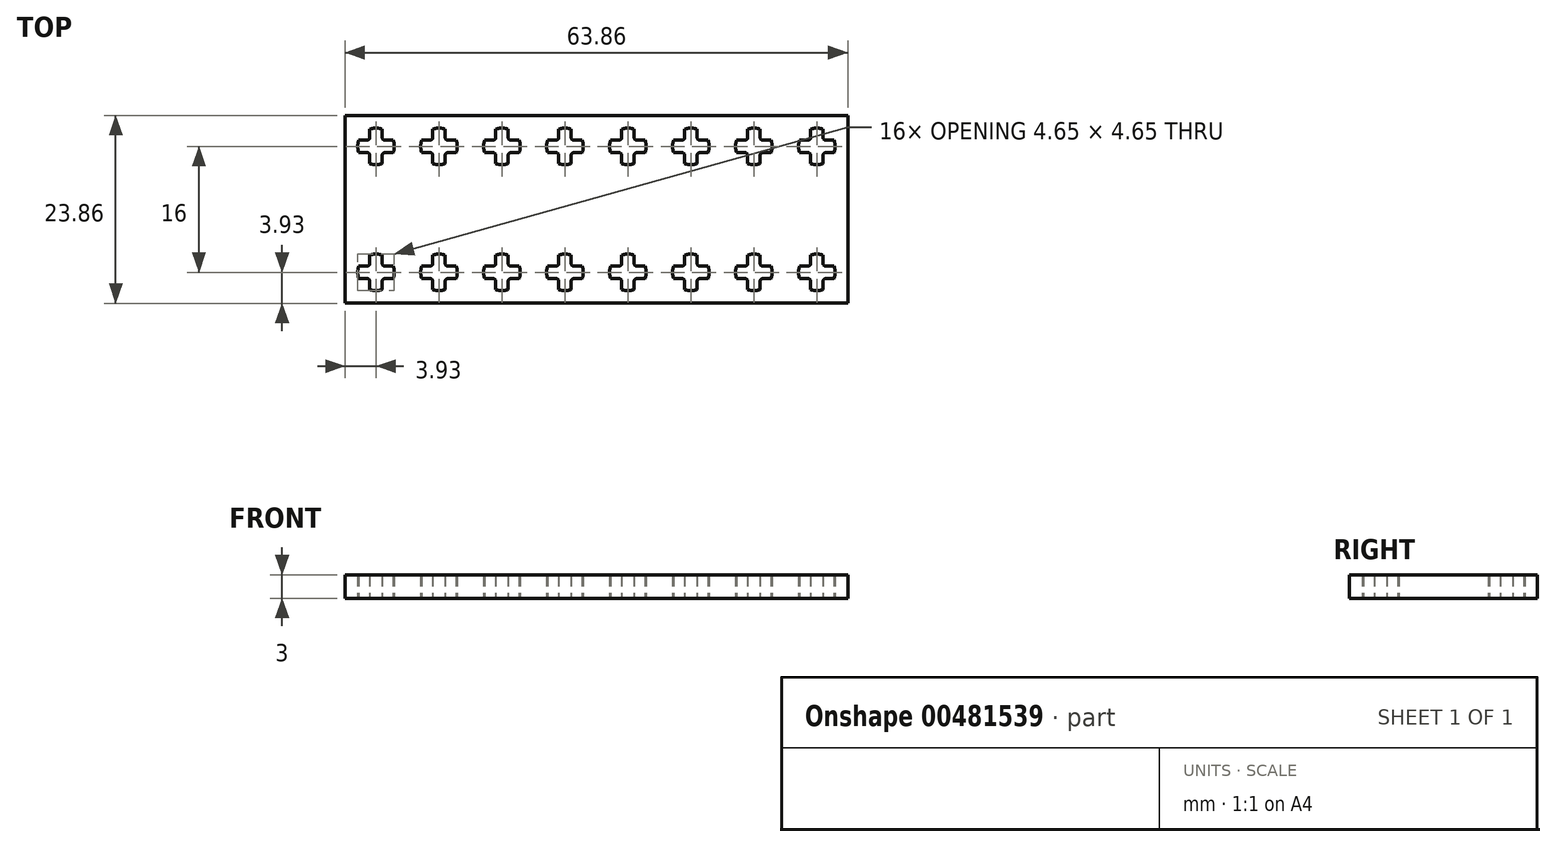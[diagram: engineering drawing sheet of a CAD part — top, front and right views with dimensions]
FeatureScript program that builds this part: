
annotation { "Feature Type Name" : "Feature", "Feature Type Description" : "" }
export const myFeature = defineFeature(function(context is Context, id is Id, definition is map)
    precondition{}
    {
        {
            var Q0;
            Q0=qCreatedBy(makeId("Top.planeOp"),FACE);
            var sketch = newSketch(context, id + "F0", { "sketchPlane" : qUnion([Q0])});
            skLineSegment(sketch, "E0.bottom", {"start": v(-32, 12) * mm, "end": v(32, 12) * mm, "construction": true});
            skLineSegment(sketch, "E0.top", {"start": v(-32, -12) * mm, "end": v(32, -12) * mm, "construction": true});
            skLineSegment(sketch, "E0.left", {"start": v(-32, 12) * mm, "end": v(-32, -12) * mm, "construction": true});
            skLineSegment(sketch, "E0.right", {"start": v(32, 12) * mm, "end": v(32, -12) * mm, "construction": true});
            skLineSegment(sketch, "E1", {"start": v(-28.8, 10.18) * mm, "end": v(-27.2, 10.18) * mm, "construction": true});
            skLineSegment(sketch, "E2", {"start": v(-27.2, 10.18) * mm, "end": v(-27.2, 9.1) * mm});
            skLineSegment(sketch, "E3", {"start": v(-26.9, 8.8) * mm, "end": v(-25.82, 8.8) * mm});
            skLineSegment(sketch, "E4", {"start": v(-25.82, 8.8) * mm, "end": v(-28, 8) * mm, "construction": true});
            skLineSegment(sketch, "E5", {"start": v(-28, 8) * mm, "end": v(-28.8, 10.18) * mm, "construction": true});
            skArc(sketch, "E6", {"start": v(-27.2, 10.18) * mm, "mid": v(-28, 10.33) * mm, "end": v(-28.8, 10.18) * mm});
            skArc(sketch, "E7", {"start": v(-27.2, 9.1) * mm, "mid": v(-27.11, 8.89) * mm, "end": v(-26.9, 8.8) * mm});
            skLineSegment(sketch, "E8", {"start": v(-27.2, 10.18) * mm, "end": v(-27.2, 8.8) * mm, "construction": true});
            skLineSegment(sketch, "E9", {"start": v(-27.2, 8.8) * mm, "end": v(-25.82, 8.8) * mm, "construction": true});
            skArc(sketch, "E10.1.0", {"start": v(-30.18, 8.8) * mm, "mid": v(-30.32, 8) * mm, "end": v(-30.18, 7.2) * mm});
            skArc(sketch, "E10.1.1", {"start": v(-29.1, 8.8) * mm, "mid": v(-28.89, 8.89) * mm, "end": v(-28.8, 9.1) * mm});
            skLineSegment(sketch, "E10.1.2", {"start": v(-30.18, 8.8) * mm, "end": v(-29.1, 8.8) * mm});
            skLineSegment(sketch, "E10.1.3", {"start": v(-28.8, 9.1) * mm, "end": v(-28.8, 10.18) * mm});
            skArc(sketch, "E10.2.0", {"start": v(-28.8, 5.82) * mm, "mid": v(-28, 5.68) * mm, "end": v(-27.2, 5.82) * mm});
            skArc(sketch, "E10.2.1", {"start": v(-28.8, 6.9) * mm, "mid": v(-28.89, 7.11) * mm, "end": v(-29.1, 7.2) * mm});
            skLineSegment(sketch, "E10.2.2", {"start": v(-28.8, 5.82) * mm, "end": v(-28.8, 6.9) * mm});
            skLineSegment(sketch, "E10.2.3", {"start": v(-29.1, 7.2) * mm, "end": v(-30.18, 7.2) * mm});
            skArc(sketch, "E10.3.0", {"start": v(-25.82, 7.2) * mm, "mid": v(-25.67, 8) * mm, "end": v(-25.82, 8.8) * mm});
            skArc(sketch, "E10.3.1", {"start": v(-26.9, 7.2) * mm, "mid": v(-27.11, 7.11) * mm, "end": v(-27.2, 6.9) * mm});
            skLineSegment(sketch, "E10.3.2", {"start": v(-25.82, 7.2) * mm, "end": v(-26.9, 7.2) * mm});
            skLineSegment(sketch, "E10.3.3", {"start": v(-27.2, 6.9) * mm, "end": v(-27.2, 5.82) * mm});
            skArc(sketch, "E11.1.0.0", {"start": v(-19.2, 10.18) * mm, "mid": v(-20, 10.32) * mm, "end": v(-20.8, 10.18) * mm});
            skArc(sketch, "E11.1.0.1", {"start": v(-18.9, 7.2) * mm, "mid": v(-19.11, 7.11) * mm, "end": v(-19.2, 6.9) * mm});
            skLineSegment(sketch, "E11.1.0.2", {"start": v(-17.82, 7.2) * mm, "end": v(-18.9, 7.2) * mm});
            skLineSegment(sketch, "E11.1.0.3", {"start": v(-21.1, 7.2) * mm, "end": v(-22.18, 7.2) * mm});
            skArc(sketch, "E11.1.0.4", {"start": v(-20.8, 6.9) * mm, "mid": v(-20.89, 7.11) * mm, "end": v(-21.1, 7.2) * mm});
            skLineSegment(sketch, "E11.1.0.5", {"start": v(-20.8, 9.1) * mm, "end": v(-20.8, 10.18) * mm});
            skLineSegment(sketch, "E11.1.0.6", {"start": v(-22.18, 8.8) * mm, "end": v(-21.1, 8.8) * mm});
            skArc(sketch, "E11.1.0.7", {"start": v(-21.1, 8.8) * mm, "mid": v(-20.89, 8.89) * mm, "end": v(-20.8, 9.1) * mm});
            skArc(sketch, "E11.1.0.8", {"start": v(-20.8, 5.82) * mm, "mid": v(-20, 5.67) * mm, "end": v(-19.2, 5.82) * mm});
            skArc(sketch, "E11.1.0.9", {"start": v(-22.18, 8.8) * mm, "mid": v(-22.32, 8) * mm, "end": v(-22.18, 7.2) * mm});
            skPoint(sketch, "E11.1.0.10", {"position": v(-20, 8) * mm});
            skLineSegment(sketch, "E11.1.0.11", {"start": v(-20.8, 5.82) * mm, "end": v(-20.8, 6.9) * mm});
            skArc(sketch, "E11.1.0.12", {"start": v(-17.82, 7.2) * mm, "mid": v(-17.67, 8) * mm, "end": v(-17.82, 8.8) * mm});
            skLineSegment(sketch, "E11.1.0.13", {"start": v(-19.2, 6.9) * mm, "end": v(-19.2, 5.82) * mm});
            skLineSegment(sketch, "E11.1.0.14", {"start": v(-19.2, 10.18) * mm, "end": v(-19.2, 9.1) * mm});
            skLineSegment(sketch, "E11.1.0.15", {"start": v(-18.9, 8.8) * mm, "end": v(-17.82, 8.8) * mm});
            skArc(sketch, "E11.1.0.16", {"start": v(-19.2, 9.1) * mm, "mid": v(-19.11, 8.89) * mm, "end": v(-18.9, 8.8) * mm});
            skArc(sketch, "E11.2.0.0", {"start": v(-11.2, 10.18) * mm, "mid": v(-12, 10.32) * mm, "end": v(-12.8, 10.18) * mm});
            skArc(sketch, "E11.2.0.1", {"start": v(-10.9, 7.2) * mm, "mid": v(-11.11, 7.11) * mm, "end": v(-11.2, 6.9) * mm});
            skLineSegment(sketch, "E11.2.0.2", {"start": v(-9.82, 7.2) * mm, "end": v(-10.9, 7.2) * mm});
            skLineSegment(sketch, "E11.2.0.3", {"start": v(-13.1, 7.2) * mm, "end": v(-14.18, 7.2) * mm});
            skArc(sketch, "E11.2.0.4", {"start": v(-12.8, 6.9) * mm, "mid": v(-12.89, 7.11) * mm, "end": v(-13.1, 7.2) * mm});
            skLineSegment(sketch, "E11.2.0.5", {"start": v(-12.8, 9.1) * mm, "end": v(-12.8, 10.18) * mm});
            skLineSegment(sketch, "E11.2.0.6", {"start": v(-14.18, 8.8) * mm, "end": v(-13.1, 8.8) * mm});
            skArc(sketch, "E11.2.0.7", {"start": v(-13.1, 8.8) * mm, "mid": v(-12.89, 8.89) * mm, "end": v(-12.8, 9.1) * mm});
            skArc(sketch, "E11.2.0.8", {"start": v(-12.8, 5.82) * mm, "mid": v(-12, 5.67) * mm, "end": v(-11.2, 5.82) * mm});
            skArc(sketch, "E11.2.0.9", {"start": v(-14.18, 8.8) * mm, "mid": v(-14.32, 8) * mm, "end": v(-14.18, 7.2) * mm});
            skPoint(sketch, "E11.2.0.10", {"position": v(-12, 8) * mm});
            skLineSegment(sketch, "E11.2.0.11", {"start": v(-12.8, 5.82) * mm, "end": v(-12.8, 6.9) * mm});
            skArc(sketch, "E11.2.0.12", {"start": v(-9.82, 7.2) * mm, "mid": v(-9.67, 8) * mm, "end": v(-9.82, 8.8) * mm});
            skLineSegment(sketch, "E11.2.0.13", {"start": v(-11.2, 6.9) * mm, "end": v(-11.2, 5.82) * mm});
            skLineSegment(sketch, "E11.2.0.14", {"start": v(-11.2, 10.18) * mm, "end": v(-11.2, 9.1) * mm});
            skLineSegment(sketch, "E11.2.0.15", {"start": v(-10.9, 8.8) * mm, "end": v(-9.82, 8.8) * mm});
            skArc(sketch, "E11.2.0.16", {"start": v(-11.2, 9.1) * mm, "mid": v(-11.11, 8.89) * mm, "end": v(-10.9, 8.8) * mm});
            skLineSegment(sketch, "E11.direction1", {"start": v(-28.8, 5.82) * mm, "end": v(-20.8, 5.82) * mm, "construction": true});
            skLineSegment(sketch, "E11.direction2", {"start": v(-28.8, 5.82) * mm, "end": v(-28.8, -2.18) * mm, "construction": true});
            skLineSegment(sketch, "E12.bottom", {"start": v(-31.92, 11.93) * mm, "end": v(31.93, 11.92) * mm});
            skLineSegment(sketch, "E12.top", {"start": v(-31.93, -11.92) * mm, "end": v(31.92, -11.93) * mm});
            skLineSegment(sketch, "E12.left", {"start": v(-31.92, 11.93) * mm, "end": v(-31.93, -11.92) * mm});
            skLineSegment(sketch, "E12.right", {"start": v(31.93, 11.92) * mm, "end": v(31.93, -11.92) * mm});
            skArc(sketch, "E13.0.3.0", {"start": v(-3.2, 10.18) * mm, "mid": v(-4, 10.32) * mm, "end": v(-4.8, 10.18) * mm});
            skArc(sketch, "E13.4.3.0", {"start": v(-2.9, 7.2) * mm, "mid": v(-3.11, 7.11) * mm, "end": v(-3.2, 6.9) * mm});
            skLineSegment(sketch, "E13.8.3.0", {"start": v(-1.82, 7.2) * mm, "end": v(-2.9, 7.2) * mm});
            skLineSegment(sketch, "E13.11.3.0", {"start": v(-5.1, 7.2) * mm, "end": v(-6.18, 7.2) * mm});
            skArc(sketch, "E13.14.3.0", {"start": v(-4.8, 6.9) * mm, "mid": v(-4.89, 7.11) * mm, "end": v(-5.1, 7.2) * mm});
            skLineSegment(sketch, "E13.18.3.0", {"start": v(-4.8, 9.1) * mm, "end": v(-4.8, 10.18) * mm});
            skLineSegment(sketch, "E13.21.3.0", {"start": v(-6.18, 8.8) * mm, "end": v(-5.1, 8.8) * mm});
            skArc(sketch, "E13.24.3.0", {"start": v(-5.1, 8.8) * mm, "mid": v(-4.89, 8.89) * mm, "end": v(-4.8, 9.1) * mm});
            skArc(sketch, "E13.28.3.0", {"start": v(-4.8, 5.82) * mm, "mid": v(-4, 5.67) * mm, "end": v(-3.2, 5.82) * mm});
            skArc(sketch, "E13.32.3.0", {"start": v(-6.18, 8.8) * mm, "mid": v(-6.32, 8) * mm, "end": v(-6.18, 7.2) * mm});
            skPoint(sketch, "E13.36.3.0", {"position": v(-4, 8) * mm});
            skLineSegment(sketch, "E13.37.3.0", {"start": v(-4.8, 5.82) * mm, "end": v(-4.8, 6.9) * mm});
            skArc(sketch, "E13.40.3.0", {"start": v(-1.82, 7.2) * mm, "mid": v(-1.67, 8) * mm, "end": v(-1.82, 8.8) * mm});
            skLineSegment(sketch, "E13.44.3.0", {"start": v(-3.2, 6.9) * mm, "end": v(-3.2, 5.82) * mm});
            skLineSegment(sketch, "E13.47.3.0", {"start": v(-3.2, 10.18) * mm, "end": v(-3.2, 9.1) * mm});
            skLineSegment(sketch, "E13.50.3.0", {"start": v(-2.9, 8.8) * mm, "end": v(-1.82, 8.8) * mm});
            skArc(sketch, "E13.53.3.0", {"start": v(-3.2, 9.1) * mm, "mid": v(-3.11, 8.89) * mm, "end": v(-2.9, 8.8) * mm});
            skArc(sketch, "E14.0.4.0", {"start": v(4.8, 10.18) * mm, "mid": v(4, 10.32) * mm, "end": v(3.2, 10.18) * mm});
            skArc(sketch, "E14.4.4.0", {"start": v(5.1, 7.2) * mm, "mid": v(4.89, 7.11) * mm, "end": v(4.8, 6.9) * mm});
            skLineSegment(sketch, "E14.8.4.0", {"start": v(6.18, 7.2) * mm, "end": v(5.1, 7.2) * mm});
            skLineSegment(sketch, "E14.11.4.0", {"start": v(2.9, 7.2) * mm, "end": v(1.82, 7.2) * mm});
            skArc(sketch, "E14.14.4.0", {"start": v(3.2, 6.9) * mm, "mid": v(3.11, 7.11) * mm, "end": v(2.9, 7.2) * mm});
            skLineSegment(sketch, "E14.18.4.0", {"start": v(3.2, 9.1) * mm, "end": v(3.2, 10.18) * mm});
            skLineSegment(sketch, "E14.21.4.0", {"start": v(1.82, 8.8) * mm, "end": v(2.9, 8.8) * mm});
            skArc(sketch, "E14.24.4.0", {"start": v(2.9, 8.8) * mm, "mid": v(3.11, 8.89) * mm, "end": v(3.2, 9.1) * mm});
            skArc(sketch, "E14.28.4.0", {"start": v(3.2, 5.82) * mm, "mid": v(4, 5.68) * mm, "end": v(4.8, 5.82) * mm});
            skArc(sketch, "E14.32.4.0", {"start": v(1.82, 8.8) * mm, "mid": v(1.68, 8) * mm, "end": v(1.82, 7.2) * mm});
            skPoint(sketch, "E14.36.4.0", {"position": v(4, 8) * mm});
            skLineSegment(sketch, "E14.37.4.0", {"start": v(3.2, 5.82) * mm, "end": v(3.2, 6.9) * mm});
            skArc(sketch, "E14.40.4.0", {"start": v(6.18, 7.2) * mm, "mid": v(6.33, 8) * mm, "end": v(6.18, 8.8) * mm});
            skLineSegment(sketch, "E14.44.4.0", {"start": v(4.8, 6.9) * mm, "end": v(4.8, 5.82) * mm});
            skLineSegment(sketch, "E14.47.4.0", {"start": v(4.8, 10.18) * mm, "end": v(4.8, 9.1) * mm});
            skLineSegment(sketch, "E14.50.4.0", {"start": v(5.1, 8.8) * mm, "end": v(6.18, 8.8) * mm});
            skArc(sketch, "E14.53.4.0", {"start": v(4.8, 9.1) * mm, "mid": v(4.89, 8.89) * mm, "end": v(5.1, 8.8) * mm});
            skLineSegment(sketch, "E15", {"start": v(-32, 8) * mm, "end": v(31.93, 8) * mm, "construction": true});
            skLineSegment(sketch, "E16", {"start": v(-28, 11.92) * mm, "end": v(-28, -12) * mm, "construction": true});
            skLineSegment(sketch, "E17.1.0.0", {"start": v(-32, 0) * mm, "end": v(31.93, 0) * mm, "construction": true});
            skLineSegment(sketch, "E17.2.0.0", {"start": v(-32, -8) * mm, "end": v(31.93, -8) * mm, "construction": true});
            skLineSegment(sketch, "E17.direction1", {"start": v(-32, 8) * mm, "end": v(-32, 0) * mm, "construction": true});
            skLineSegment(sketch, "E18.0.1.0", {"start": v(-20, 11.92) * mm, "end": v(-20, -12) * mm, "construction": true});
            skLineSegment(sketch, "E18.0.2.0", {"start": v(-12, 11.92) * mm, "end": v(-12, -12) * mm, "construction": true});
            skLineSegment(sketch, "E18.0.3.0", {"start": v(-4, 11.92) * mm, "end": v(-4, -12) * mm, "construction": true});
            skLineSegment(sketch, "E18.0.4.0", {"start": v(4, 11.92) * mm, "end": v(4, -12) * mm, "construction": true});
            skLineSegment(sketch, "E18.direction1", {"start": v(-28, -12) * mm, "end": v(-19.3, -12) * mm, "construction": true});
            skLineSegment(sketch, "E18.direction2", {"start": v(-28, -12) * mm, "end": v(-20, -12) * mm, "construction": true});
            skArc(sketch, "E19.0.5.0", {"start": v(12.8, 10.18) * mm, "mid": v(12, 10.32) * mm, "end": v(11.2, 10.18) * mm});
            skArc(sketch, "E19.4.5.0", {"start": v(13.1, 7.2) * mm, "mid": v(12.89, 7.11) * mm, "end": v(12.8, 6.9) * mm});
            skLineSegment(sketch, "E19.8.5.0", {"start": v(14.18, 7.2) * mm, "end": v(13.1, 7.2) * mm});
            skLineSegment(sketch, "E19.11.5.0", {"start": v(10.9, 7.2) * mm, "end": v(9.82, 7.2) * mm});
            skArc(sketch, "E19.14.5.0", {"start": v(11.2, 6.9) * mm, "mid": v(11.11, 7.11) * mm, "end": v(10.9, 7.2) * mm});
            skLineSegment(sketch, "E19.18.5.0", {"start": v(11.2, 9.1) * mm, "end": v(11.2, 10.18) * mm});
            skLineSegment(sketch, "E19.21.5.0", {"start": v(9.82, 8.8) * mm, "end": v(10.9, 8.8) * mm});
            skArc(sketch, "E19.24.5.0", {"start": v(10.9, 8.8) * mm, "mid": v(11.11, 8.89) * mm, "end": v(11.2, 9.1) * mm});
            skArc(sketch, "E19.28.5.0", {"start": v(11.2, 5.82) * mm, "mid": v(12, 5.67) * mm, "end": v(12.8, 5.82) * mm});
            skArc(sketch, "E19.32.5.0", {"start": v(9.82, 8.8) * mm, "mid": v(9.68, 8) * mm, "end": v(9.82, 7.2) * mm});
            skPoint(sketch, "E19.36.5.0", {"position": v(12, 8) * mm});
            skLineSegment(sketch, "E19.37.5.0", {"start": v(11.2, 5.82) * mm, "end": v(11.2, 6.9) * mm});
            skArc(sketch, "E19.40.5.0", {"start": v(14.18, 7.2) * mm, "mid": v(14.33, 8) * mm, "end": v(14.18, 8.8) * mm});
            skLineSegment(sketch, "E19.44.5.0", {"start": v(12.8, 6.9) * mm, "end": v(12.8, 5.82) * mm});
            skLineSegment(sketch, "E19.47.5.0", {"start": v(12.8, 10.18) * mm, "end": v(12.8, 9.1) * mm});
            skLineSegment(sketch, "E19.50.5.0", {"start": v(13.1, 8.8) * mm, "end": v(14.18, 8.8) * mm});
            skArc(sketch, "E19.53.5.0", {"start": v(12.8, 9.1) * mm, "mid": v(12.89, 8.89) * mm, "end": v(13.1, 8.8) * mm});
            skArc(sketch, "E20.0.6.0", {"start": v(20.8, 10.18) * mm, "mid": v(20, 10.32) * mm, "end": v(19.2, 10.18) * mm});
            skArc(sketch, "E20.4.6.0", {"start": v(21.1, 7.2) * mm, "mid": v(20.89, 7.11) * mm, "end": v(20.8, 6.9) * mm});
            skLineSegment(sketch, "E20.8.6.0", {"start": v(22.18, 7.2) * mm, "end": v(21.1, 7.2) * mm});
            skLineSegment(sketch, "E20.11.6.0", {"start": v(18.9, 7.2) * mm, "end": v(17.82, 7.2) * mm});
            skArc(sketch, "E20.14.6.0", {"start": v(19.2, 6.9) * mm, "mid": v(19.11, 7.11) * mm, "end": v(18.9, 7.2) * mm});
            skLineSegment(sketch, "E20.18.6.0", {"start": v(19.2, 9.1) * mm, "end": v(19.2, 10.18) * mm});
            skLineSegment(sketch, "E20.21.6.0", {"start": v(17.82, 8.8) * mm, "end": v(18.9, 8.8) * mm});
            skArc(sketch, "E20.24.6.0", {"start": v(18.9, 8.8) * mm, "mid": v(19.11, 8.89) * mm, "end": v(19.2, 9.1) * mm});
            skArc(sketch, "E20.28.6.0", {"start": v(19.2, 5.82) * mm, "mid": v(20, 5.67) * mm, "end": v(20.8, 5.82) * mm});
            skArc(sketch, "E20.32.6.0", {"start": v(17.82, 8.8) * mm, "mid": v(17.68, 8) * mm, "end": v(17.82, 7.2) * mm});
            skPoint(sketch, "E20.36.6.0", {"position": v(20, 8) * mm});
            skLineSegment(sketch, "E20.37.6.0", {"start": v(19.2, 5.82) * mm, "end": v(19.2, 6.9) * mm});
            skArc(sketch, "E20.40.6.0", {"start": v(22.18, 7.2) * mm, "mid": v(22.33, 8) * mm, "end": v(22.18, 8.8) * mm});
            skLineSegment(sketch, "E20.44.6.0", {"start": v(20.8, 6.9) * mm, "end": v(20.8, 5.82) * mm});
            skLineSegment(sketch, "E20.47.6.0", {"start": v(20.8, 10.18) * mm, "end": v(20.8, 9.1) * mm});
            skLineSegment(sketch, "E20.50.6.0", {"start": v(21.1, 8.8) * mm, "end": v(22.18, 8.8) * mm});
            skArc(sketch, "E20.53.6.0", {"start": v(20.8, 9.1) * mm, "mid": v(20.89, 8.89) * mm, "end": v(21.1, 8.8) * mm});
            skArc(sketch, "E20.0.7.0", {"start": v(28.8, 10.18) * mm, "mid": v(28, 10.32) * mm, "end": v(27.2, 10.18) * mm});
            skArc(sketch, "E20.4.7.0", {"start": v(29.1, 7.2) * mm, "mid": v(28.89, 7.11) * mm, "end": v(28.8, 6.9) * mm});
            skLineSegment(sketch, "E20.8.7.0", {"start": v(30.18, 7.2) * mm, "end": v(29.1, 7.2) * mm});
            skLineSegment(sketch, "E20.11.7.0", {"start": v(26.9, 7.2) * mm, "end": v(25.82, 7.2) * mm});
            skArc(sketch, "E20.14.7.0", {"start": v(27.2, 6.9) * mm, "mid": v(27.11, 7.11) * mm, "end": v(26.9, 7.2) * mm});
            skLineSegment(sketch, "E20.18.7.0", {"start": v(27.2, 9.1) * mm, "end": v(27.2, 10.18) * mm});
            skLineSegment(sketch, "E20.21.7.0", {"start": v(25.82, 8.8) * mm, "end": v(26.9, 8.8) * mm});
            skArc(sketch, "E20.24.7.0", {"start": v(26.9, 8.8) * mm, "mid": v(27.11, 8.89) * mm, "end": v(27.2, 9.1) * mm});
            skArc(sketch, "E20.28.7.0", {"start": v(27.2, 5.82) * mm, "mid": v(28, 5.67) * mm, "end": v(28.8, 5.82) * mm});
            skArc(sketch, "E20.32.7.0", {"start": v(25.82, 8.8) * mm, "mid": v(25.68, 8) * mm, "end": v(25.82, 7.2) * mm});
            skPoint(sketch, "E20.36.7.0", {"position": v(28, 8) * mm});
            skLineSegment(sketch, "E20.37.7.0", {"start": v(27.2, 5.82) * mm, "end": v(27.2, 6.9) * mm});
            skArc(sketch, "E20.40.7.0", {"start": v(30.18, 7.2) * mm, "mid": v(30.33, 8) * mm, "end": v(30.18, 8.8) * mm});
            skLineSegment(sketch, "E20.44.7.0", {"start": v(28.8, 6.9) * mm, "end": v(28.8, 5.82) * mm});
            skLineSegment(sketch, "E20.47.7.0", {"start": v(28.8, 10.18) * mm, "end": v(28.8, 9.1) * mm});
            skLineSegment(sketch, "E20.50.7.0", {"start": v(29.1, 8.8) * mm, "end": v(30.18, 8.8) * mm});
            skArc(sketch, "E20.53.7.0", {"start": v(28.8, 9.1) * mm, "mid": v(28.89, 8.89) * mm, "end": v(29.1, 8.8) * mm});
            skLineSegment(sketch, "E21.MirrorCS", {"start": v(-27.2, -10.18) * mm, "end": v(-27.2, -9.1) * mm});
            skArc(sketch, "E22.MirrorCS", {"start": v(-20.8, -6.9) * mm, "mid": v(-20.89, -7.11) * mm, "end": v(-21.1, -7.2) * mm});
            skArc(sketch, "E23.MirrorCS", {"start": v(-2.9, -7.2) * mm, "mid": v(-3.11, -7.11) * mm, "end": v(-3.2, -6.9) * mm});
            skArc(sketch, "E24.MirrorCS", {"start": v(-18.9, -7.2) * mm, "mid": v(-19.11, -7.11) * mm, "end": v(-19.2, -6.9) * mm});
            skArc(sketch, "E25.MirrorCS", {"start": v(29.1, -7.2) * mm, "mid": v(28.89, -7.11) * mm, "end": v(28.8, -6.9) * mm});
            skArc(sketch, "E26.MirrorCS", {"start": v(13.1, -7.2) * mm, "mid": v(12.89, -7.11) * mm, "end": v(12.8, -6.9) * mm});
            skLineSegment(sketch, "E27.MirrorCS", {"start": v(-25.82, -8.8) * mm, "end": v(-28, -8) * mm, "construction": true});
            skArc(sketch, "E28.MirrorCS", {"start": v(-27.2, -9.1) * mm, "mid": v(-27.11, -8.89) * mm, "end": v(-26.9, -8.8) * mm});
            skLineSegment(sketch, "E29.MirrorCS", {"start": v(-26.9, -8.8) * mm, "end": v(-25.82, -8.8) * mm});
            skLineSegment(sketch, "E30.MirrorCS", {"start": v(-28.8, -10.18) * mm, "end": v(-27.2, -10.18) * mm, "construction": true});
            skArc(sketch, "E31.MirrorCS", {"start": v(5.1, -7.2) * mm, "mid": v(4.89, -7.11) * mm, "end": v(4.8, -6.9) * mm});
            skArc(sketch, "E32.MirrorCS", {"start": v(3.2, -6.9) * mm, "mid": v(3.11, -7.11) * mm, "end": v(2.9, -7.2) * mm});
            skArc(sketch, "E33.MirrorCS", {"start": v(-19.2, -9.1) * mm, "mid": v(-19.11, -8.89) * mm, "end": v(-18.9, -8.8) * mm});
            skArc(sketch, "E34.MirrorCS", {"start": v(27.2, -6.9) * mm, "mid": v(27.11, -7.11) * mm, "end": v(26.9, -7.2) * mm});
            skArc(sketch, "E35.MirrorCS", {"start": v(21.1, -7.2) * mm, "mid": v(20.89, -7.11) * mm, "end": v(20.8, -6.9) * mm});
            skArc(sketch, "E36.MirrorCS", {"start": v(-28.8, -6.9) * mm, "mid": v(-28.89, -7.11) * mm, "end": v(-29.1, -7.2) * mm});
            skLineSegment(sketch, "E37.MirrorCS", {"start": v(-28.8, -5.82) * mm, "end": v(-28.8, -6.9) * mm});
            skLineSegment(sketch, "E38.MirrorCS", {"start": v(-27.2, -8.8) * mm, "end": v(-25.82, -8.8) * mm, "construction": true});
            skArc(sketch, "E39.MirrorCS", {"start": v(-27.2, -10.18) * mm, "mid": v(-28, -10.32) * mm, "end": v(-28.8, -10.18) * mm});
            skArc(sketch, "E40.MirrorCS", {"start": v(11.2, -6.9) * mm, "mid": v(11.11, -7.11) * mm, "end": v(10.9, -7.2) * mm});
            skLineSegment(sketch, "E41.MirrorCS", {"start": v(-27.2, -10.18) * mm, "end": v(-27.2, -8.8) * mm, "construction": true});
            skArc(sketch, "E42.MirrorCS", {"start": v(28.8, -9.1) * mm, "mid": v(28.89, -8.89) * mm, "end": v(29.1, -8.8) * mm});
            skLineSegment(sketch, "E43.MirrorCS", {"start": v(-11.2, -10.18) * mm, "end": v(-11.2, -9.1) * mm});
            skArc(sketch, "E44.MirrorCS", {"start": v(12.8, -9.1) * mm, "mid": v(12.89, -8.89) * mm, "end": v(13.1, -8.8) * mm});
            skArc(sketch, "E45.MirrorCS", {"start": v(-3.2, -9.1) * mm, "mid": v(-3.11, -8.89) * mm, "end": v(-2.9, -8.8) * mm});
            skLineSegment(sketch, "E46.MirrorCS", {"start": v(20.8, -10.18) * mm, "end": v(20.8, -9.1) * mm});
            skLineSegment(sketch, "E47.MirrorCS", {"start": v(-20.8, -5.82) * mm, "end": v(-20.8, -6.9) * mm});
            skArc(sketch, "E48.MirrorCS", {"start": v(-21.1, -8.8) * mm, "mid": v(-20.89, -8.89) * mm, "end": v(-20.8, -9.1) * mm});
            skArc(sketch, "E49.MirrorCS", {"start": v(18.9, -8.8) * mm, "mid": v(19.11, -8.89) * mm, "end": v(19.2, -9.1) * mm});
            skArc(sketch, "E50.MirrorCS", {"start": v(20.8, -9.1) * mm, "mid": v(20.89, -8.89) * mm, "end": v(21.1, -8.8) * mm});
            skArc(sketch, "E51.MirrorCS", {"start": v(-4.8, -6.9) * mm, "mid": v(-4.89, -7.11) * mm, "end": v(-5.1, -7.2) * mm});
            skArc(sketch, "E52.MirrorCS", {"start": v(-12.8, -6.9) * mm, "mid": v(-12.89, -7.11) * mm, "end": v(-13.1, -7.2) * mm});
            skArc(sketch, "E53.MirrorCS", {"start": v(-10.9, -7.2) * mm, "mid": v(-11.11, -7.11) * mm, "end": v(-11.2, -6.9) * mm});
            skArc(sketch, "E54.MirrorCS", {"start": v(2.9, -8.8) * mm, "mid": v(3.11, -8.89) * mm, "end": v(3.2, -9.1) * mm});
            skArc(sketch, "E55.MirrorCS", {"start": v(19.2, -6.9) * mm, "mid": v(19.11, -7.11) * mm, "end": v(18.9, -7.2) * mm});
            skArc(sketch, "E56.MirrorCS", {"start": v(-26.9, -7.2) * mm, "mid": v(-27.11, -7.11) * mm, "end": v(-27.2, -6.9) * mm});
            skLineSegment(sketch, "E57.MirrorCS", {"start": v(-28.8, -9.1) * mm, "end": v(-28.8, -10.18) * mm});
            skLineSegment(sketch, "E58.MirrorCS", {"start": v(3.2, -9.1) * mm, "end": v(3.2, -10.18) * mm});
            skLineSegment(sketch, "E59.MirrorCS", {"start": v(-28.8, -5.82) * mm, "end": v(-20.8, -5.82) * mm, "construction": true});
            skLineSegment(sketch, "E60.MirrorCS", {"start": v(-28, -8) * mm, "end": v(-28.8, -10.18) * mm, "construction": true});
            skArc(sketch, "E61.MirrorCS", {"start": v(-11.2, -9.1) * mm, "mid": v(-11.11, -8.89) * mm, "end": v(-10.9, -8.8) * mm});
            skArc(sketch, "E62.MirrorCS", {"start": v(-29.1, -8.8) * mm, "mid": v(-28.89, -8.89) * mm, "end": v(-28.8, -9.1) * mm});
            skArc(sketch, "E63.MirrorCS", {"start": v(9.82, -8.8) * mm, "mid": v(9.68, -8) * mm, "end": v(9.82, -7.2) * mm});
            skLineSegment(sketch, "E64.MirrorCS", {"start": v(26.9, -7.2) * mm, "end": v(25.82, -7.2) * mm});
            skLineSegment(sketch, "E65.MirrorCS", {"start": v(22.18, -7.2) * mm, "end": v(21.1, -7.2) * mm});
            skArc(sketch, "E66.MirrorCS", {"start": v(28.8, -10.18) * mm, "mid": v(28, -10.32) * mm, "end": v(27.2, -10.18) * mm});
            skLineSegment(sketch, "E67.MirrorCS", {"start": v(-3.2, -6.9) * mm, "end": v(-3.2, -5.82) * mm});
            skArc(sketch, "E68.MirrorCS", {"start": v(1.82, -8.8) * mm, "mid": v(1.68, -8) * mm, "end": v(1.82, -7.2) * mm});
            skArc(sketch, "E69.MirrorCS", {"start": v(30.18, -7.2) * mm, "mid": v(30.33, -8) * mm, "end": v(30.18, -8.8) * mm});
            skLineSegment(sketch, "E70.MirrorCS", {"start": v(4.8, -6.9) * mm, "end": v(4.8, -5.82) * mm});
            skLineSegment(sketch, "E71.MirrorCS", {"start": v(18.9, -7.2) * mm, "end": v(17.82, -7.2) * mm});
            skLineSegment(sketch, "E72.MirrorCS", {"start": v(-10.9, -8.8) * mm, "end": v(-9.82, -8.8) * mm});
            skLineSegment(sketch, "E73.MirrorCS", {"start": v(11.2, -5.82) * mm, "end": v(11.2, -6.9) * mm});
            skLineSegment(sketch, "E74.MirrorCS", {"start": v(4.8, -10.18) * mm, "end": v(4.8, -9.1) * mm});
            skArc(sketch, "E75.MirrorCS", {"start": v(11.2, -5.82) * mm, "mid": v(12, -5.68) * mm, "end": v(12.8, -5.82) * mm});
            skArc(sketch, "E76.MirrorCS", {"start": v(22.18, -7.2) * mm, "mid": v(22.33, -8) * mm, "end": v(22.18, -8.8) * mm});
            skArc(sketch, "E77.MirrorCS", {"start": v(-13.1, -8.8) * mm, "mid": v(-12.89, -8.89) * mm, "end": v(-12.8, -9.1) * mm});
            skArc(sketch, "E78.MirrorCS", {"start": v(-25.82, -7.2) * mm, "mid": v(-25.67, -8) * mm, "end": v(-25.82, -8.8) * mm});
            skLineSegment(sketch, "E79.MirrorCS", {"start": v(1.82, -8.8) * mm, "end": v(2.9, -8.8) * mm});
            skLineSegment(sketch, "E80.MirrorCS", {"start": v(-29.1, -7.2) * mm, "end": v(-30.18, -7.2) * mm});
            skLineSegment(sketch, "E81.MirrorCS", {"start": v(-13.1, -7.2) * mm, "end": v(-14.18, -7.2) * mm});
            skLineSegment(sketch, "E82.MirrorCS", {"start": v(27.2, -5.82) * mm, "end": v(27.2, -6.9) * mm});
            skLineSegment(sketch, "E83.MirrorCS", {"start": v(-27.2, -6.9) * mm, "end": v(-27.2, -5.82) * mm});
            skArc(sketch, "E84.MirrorCS", {"start": v(25.82, -8.8) * mm, "mid": v(25.68, -8) * mm, "end": v(25.82, -7.2) * mm});
            skLineSegment(sketch, "E85.MirrorCS", {"start": v(28.8, -10.18) * mm, "end": v(28.8, -9.1) * mm});
            skArc(sketch, "E86.MirrorCS", {"start": v(-1.82, -7.2) * mm, "mid": v(-1.67, -8) * mm, "end": v(-1.82, -8.8) * mm});
            skLineSegment(sketch, "E87.MirrorCS", {"start": v(-19.2, -10.18) * mm, "end": v(-19.2, -9.1) * mm});
            skLineSegment(sketch, "E88.MirrorCS", {"start": v(-21.1, -7.2) * mm, "end": v(-22.18, -7.2) * mm});
            skLineSegment(sketch, "E89.MirrorCS", {"start": v(29.1, -8.8) * mm, "end": v(30.18, -8.8) * mm});
            skLineSegment(sketch, "E90.MirrorCS", {"start": v(25.82, -8.8) * mm, "end": v(26.9, -8.8) * mm});
            skArc(sketch, "E91.MirrorCS", {"start": v(-5.1, -8.8) * mm, "mid": v(-4.89, -8.89) * mm, "end": v(-4.8, -9.1) * mm});
            skLineSegment(sketch, "E92.MirrorCS", {"start": v(12.8, -6.9) * mm, "end": v(12.8, -5.82) * mm});
            skArc(sketch, "E93.MirrorCS", {"start": v(-14.18, -8.8) * mm, "mid": v(-14.32, -8) * mm, "end": v(-14.18, -7.2) * mm});
            skLineSegment(sketch, "E94.MirrorCS", {"start": v(-4.8, -9.1) * mm, "end": v(-4.8, -10.18) * mm});
            skLineSegment(sketch, "E95.MirrorCS", {"start": v(14.18, -7.2) * mm, "end": v(13.1, -7.2) * mm});
            skLineSegment(sketch, "E96.MirrorCS", {"start": v(-5.1, -7.2) * mm, "end": v(-6.18, -7.2) * mm});
            skLineSegment(sketch, "E97.MirrorCS", {"start": v(-9.82, -7.2) * mm, "end": v(-10.9, -7.2) * mm});
            skArc(sketch, "E98.MirrorCS", {"start": v(27.2, -5.82) * mm, "mid": v(28, -5.67) * mm, "end": v(28.8, -5.82) * mm});
            skArc(sketch, "E99.MirrorCS", {"start": v(-19.2, -10.18) * mm, "mid": v(-20, -10.32) * mm, "end": v(-20.8, -10.18) * mm});
            skArc(sketch, "E100.MirrorCS", {"start": v(-17.82, -7.2) * mm, "mid": v(-17.67, -8) * mm, "end": v(-17.82, -8.8) * mm});
            skArc(sketch, "E101.MirrorCS", {"start": v(-3.2, -10.18) * mm, "mid": v(-4, -10.32) * mm, "end": v(-4.8, -10.18) * mm});
            skArc(sketch, "E102.MirrorCS", {"start": v(17.82, -8.8) * mm, "mid": v(17.68, -8) * mm, "end": v(17.82, -7.2) * mm});
            skLineSegment(sketch, "E103.MirrorCS", {"start": v(10.9, -7.2) * mm, "end": v(9.82, -7.2) * mm});
            skLineSegment(sketch, "E104.MirrorCS", {"start": v(-19.2, -6.9) * mm, "end": v(-19.2, -5.82) * mm});
            skLineSegment(sketch, "E105.MirrorCS", {"start": v(21.1, -8.8) * mm, "end": v(22.18, -8.8) * mm});
            skLineSegment(sketch, "E106.MirrorCS", {"start": v(-12.8, -5.82) * mm, "end": v(-12.8, -6.9) * mm});
            skArc(sketch, "E107.MirrorCS", {"start": v(4.8, -9.1) * mm, "mid": v(4.89, -8.89) * mm, "end": v(5.1, -8.8) * mm});
            skLineSegment(sketch, "E108.MirrorCS", {"start": v(3.2, -5.82) * mm, "end": v(3.2, -6.9) * mm});
            skLineSegment(sketch, "E109.MirrorCS", {"start": v(-22.18, -8.8) * mm, "end": v(-21.1, -8.8) * mm});
            skArc(sketch, "E110.MirrorCS", {"start": v(4.8, -10.18) * mm, "mid": v(4, -10.33) * mm, "end": v(3.2, -10.18) * mm});
            skArc(sketch, "E111.MirrorCS", {"start": v(-12.8, -5.82) * mm, "mid": v(-12, -5.67) * mm, "end": v(-11.2, -5.82) * mm});
            skArc(sketch, "E112.MirrorCS", {"start": v(19.2, -5.82) * mm, "mid": v(20, -5.67) * mm, "end": v(20.8, -5.82) * mm});
            skArc(sketch, "E113.MirrorCS", {"start": v(6.18, -7.2) * mm, "mid": v(6.33, -8) * mm, "end": v(6.18, -8.8) * mm});
            skLineSegment(sketch, "E114.MirrorCS", {"start": v(17.82, -8.8) * mm, "end": v(18.9, -8.8) * mm});
            skLineSegment(sketch, "E115.MirrorCS", {"start": v(-1.82, -7.2) * mm, "end": v(-2.9, -7.2) * mm});
            skLineSegment(sketch, "E116.MirrorCS", {"start": v(-2.9, -8.8) * mm, "end": v(-1.82, -8.8) * mm});
            skArc(sketch, "E117.MirrorCS", {"start": v(-22.18, -8.8) * mm, "mid": v(-22.32, -8) * mm, "end": v(-22.18, -7.2) * mm});
            skLineSegment(sketch, "E118.MirrorCS", {"start": v(-6.18, -8.8) * mm, "end": v(-5.1, -8.8) * mm});
            skLineSegment(sketch, "E119.MirrorCS", {"start": v(-20.8, -9.1) * mm, "end": v(-20.8, -10.18) * mm});
            skArc(sketch, "E120.MirrorCS", {"start": v(-6.18, -8.8) * mm, "mid": v(-6.32, -8) * mm, "end": v(-6.18, -7.2) * mm});
            skArc(sketch, "E121.MirrorCS", {"start": v(-11.2, -10.18) * mm, "mid": v(-12, -10.32) * mm, "end": v(-12.8, -10.18) * mm});
            skArc(sketch, "E122.MirrorCS", {"start": v(26.9, -8.8) * mm, "mid": v(27.11, -8.89) * mm, "end": v(27.2, -9.1) * mm});
            skArc(sketch, "E123.MirrorCS", {"start": v(-20.8, -5.82) * mm, "mid": v(-20, -5.67) * mm, "end": v(-19.2, -5.82) * mm});
            skLineSegment(sketch, "E124.MirrorCS", {"start": v(27.2, -9.1) * mm, "end": v(27.2, -10.18) * mm});
            skArc(sketch, "E125.MirrorCS", {"start": v(12.8, -10.18) * mm, "mid": v(12, -10.32) * mm, "end": v(11.2, -10.18) * mm});
            skLineSegment(sketch, "E126.MirrorCS", {"start": v(9.82, -8.8) * mm, "end": v(10.9, -8.8) * mm});
            skLineSegment(sketch, "E127.MirrorCS", {"start": v(6.18, -7.2) * mm, "end": v(5.1, -7.2) * mm});
            skLineSegment(sketch, "E128.MirrorCS", {"start": v(-17.82, -7.2) * mm, "end": v(-18.9, -7.2) * mm});
            skLineSegment(sketch, "E129.MirrorCS", {"start": v(-12.8, -9.1) * mm, "end": v(-12.8, -10.18) * mm});
            skLineSegment(sketch, "E130.MirrorCS", {"start": v(5.1, -8.8) * mm, "end": v(6.18, -8.8) * mm});
            skLineSegment(sketch, "E131.MirrorCS", {"start": v(20.8, -6.9) * mm, "end": v(20.8, -5.82) * mm});
            skLineSegment(sketch, "E132.MirrorCS", {"start": v(-3.2, -10.18) * mm, "end": v(-3.2, -9.1) * mm});
            skLineSegment(sketch, "E133.MirrorCS", {"start": v(2.9, -7.2) * mm, "end": v(1.82, -7.2) * mm});
            skLineSegment(sketch, "E134.MirrorCS", {"start": v(19.2, -5.82) * mm, "end": v(19.2, -6.9) * mm});
            skLineSegment(sketch, "E135.MirrorCS", {"start": v(-11.2, -6.9) * mm, "end": v(-11.2, -5.82) * mm});
            skLineSegment(sketch, "E136.MirrorCS", {"start": v(-4.8, -5.82) * mm, "end": v(-4.8, -6.9) * mm});
            skArc(sketch, "E137.MirrorCS", {"start": v(20.8, -10.18) * mm, "mid": v(20, -10.32) * mm, "end": v(19.2, -10.18) * mm});
            skArc(sketch, "E138.MirrorCS", {"start": v(14.18, -7.2) * mm, "mid": v(14.33, -8) * mm, "end": v(14.18, -8.8) * mm});
            skLineSegment(sketch, "E139.MirrorCS", {"start": v(11.2, -9.1) * mm, "end": v(11.2, -10.18) * mm});
            skLineSegment(sketch, "E140.MirrorCS", {"start": v(12.8, -10.18) * mm, "end": v(12.8, -9.1) * mm});
            skLineSegment(sketch, "E141.MirrorCS", {"start": v(28.8, -6.9) * mm, "end": v(28.8, -5.82) * mm});
            skLineSegment(sketch, "E142.MirrorCS", {"start": v(19.2, -9.1) * mm, "end": v(19.2, -10.18) * mm});
            skLineSegment(sketch, "E143.MirrorCS", {"start": v(-18.9, -8.8) * mm, "end": v(-17.82, -8.8) * mm});
            skArc(sketch, "E144.MirrorCS", {"start": v(-4.8, -5.82) * mm, "mid": v(-4, -5.67) * mm, "end": v(-3.2, -5.82) * mm});
            skArc(sketch, "E145.MirrorCS", {"start": v(10.9, -8.8) * mm, "mid": v(11.11, -8.89) * mm, "end": v(11.2, -9.1) * mm});
            skArc(sketch, "E146.MirrorCS", {"start": v(3.2, -5.82) * mm, "mid": v(4, -5.68) * mm, "end": v(4.8, -5.82) * mm});
            skArc(sketch, "E147.MirrorCS", {"start": v(-9.82, -7.2) * mm, "mid": v(-9.67, -8) * mm, "end": v(-9.82, -8.8) * mm});
            skLineSegment(sketch, "E148.MirrorCS", {"start": v(-25.82, -7.2) * mm, "end": v(-26.9, -7.2) * mm});
            skArc(sketch, "E149.MirrorCS", {"start": v(-30.18, -8.8) * mm, "mid": v(-30.32, -8) * mm, "end": v(-30.18, -7.2) * mm});
            skArc(sketch, "E150.MirrorCS", {"start": v(-28.8, -5.82) * mm, "mid": v(-28, -5.67) * mm, "end": v(-27.2, -5.82) * mm});
            skLineSegment(sketch, "E151.MirrorCS", {"start": v(-30.18, -8.8) * mm, "end": v(-29.1, -8.8) * mm});
            skLineSegment(sketch, "E152.MirrorCS", {"start": v(13.1, -8.8) * mm, "end": v(14.18, -8.8) * mm});
            skLineSegment(sketch, "E153.MirrorCS", {"start": v(30.18, -7.2) * mm, "end": v(29.1, -7.2) * mm});
            skLineSegment(sketch, "E154.MirrorCS", {"start": v(-14.18, -8.8) * mm, "end": v(-13.1, -8.8) * mm});
            skLineSegment(sketch, "E155.0.0.5", {"start": v(12, 11.92) * mm, "end": v(12, -12) * mm, "construction": true});
            skLineSegment(sketch, "E155.0.0.6", {"start": v(20, 11.92) * mm, "end": v(20, -12) * mm, "construction": true});
            skLineSegment(sketch, "E155.0.0.7", {"start": v(28, 11.92) * mm, "end": v(28, -12) * mm, "construction": true});
            skSolve(sketch);
        }
        {
            var Q0;
            Q0=makeQuery(id+"F0.imprint","IMPRINT",FACE,{"disambiguationData":[TD([[makeQuery(id+"F0.imprint","IMPRINT",EDGE,{"derivedFrom":sQuery(id+"F0.wireOp",EDGE,"E2")}),1.0]])]});
            extrude(context, id + "F1", {"entities" : qUnion([Q0]), "depth" : 3 * mm, "offsetDistance" : 25 * mm});
        }
    });
